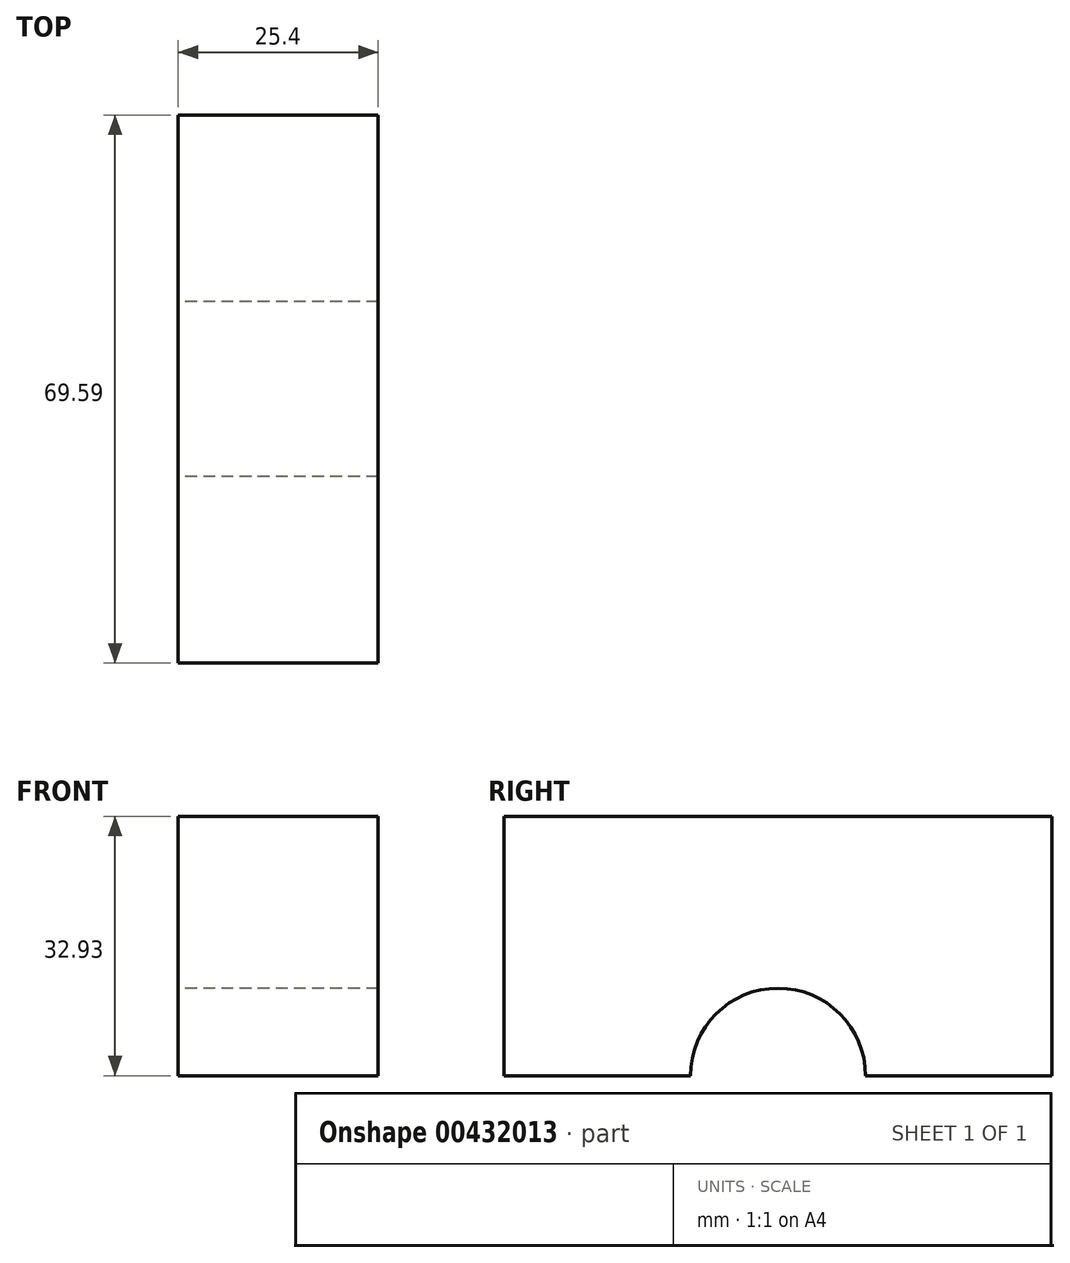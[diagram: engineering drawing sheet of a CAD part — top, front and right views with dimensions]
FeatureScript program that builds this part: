
annotation { "Feature Type Name" : "Feature", "Feature Type Description" : "" }
export const myFeature = defineFeature(function(context is Context, id is Id, definition is map)
    precondition{}
    {
        {
            var Q0;
            Q0=qCreatedBy(makeId("Right.planeOp"),FACE);
            var sketch = newSketch(context, id + "F0", { "sketchPlane" : qUnion([Q0])});
            skLineSegment(sketch, "E0.bottom", {"start": v(0, 0) * mm, "end": v(69.59, 0) * mm});
            skLineSegment(sketch, "E0.top", {"start": v(0, 32.93) * mm, "end": v(69.59, 32.93) * mm});
            skLineSegment(sketch, "E0.left", {"start": v(0, 0) * mm, "end": v(0, 32.93) * mm});
            skLineSegment(sketch, "E0.right", {"start": v(69.59, 0) * mm, "end": v(69.59, 32.93) * mm});
            skSolve(sketch);
        }
        {
            var Q0;
            Q0 = qSketchRegion(id + "F0", true);
            extrude(context, id + "F1", {"entities" : qUnion([Q0]), "depth" : 25.4 * mm});
        }
        {
            var Q0;
            Q0=makeQuery(id+"F1.opExtrude","CAP_FACE",FACE,{"disambiguationData":[OSD([sQuery(id+"F0.wireOp",EDGE,"E0.bottom"),sQuery(id+"F0.wireOp",EDGE,"E0.top"),sQuery(id+"F0.wireOp",EDGE,"E0.left"),sQuery(id+"F0.wireOp",EDGE,"E0.right")])],"isStart":true});
            var sketch = newSketch(context, id + "F2", { "sketchPlane" : qUnion([Q0])});
            skLineSegment(sketch, "E1", {"start": v(-34.8, 0) * mm, "end": v(-34.8, 3.7) * mm});
            skSolve(sketch);
        }
        {
            var Q0;
            Q0=sQuery(id+"F2.wireOp",VERTEX,"E1.start");
            var Q1;
            Q1=makeQuery(id+"F1.opExtrude","SWEPT_BODY",BODY,{"disambiguationData":[OSD([sQuery(id+"F0.wireOp",EDGE,"E0.bottom"),sQuery(id+"F0.wireOp",EDGE,"E0.top"),sQuery(id+"F0.wireOp",EDGE,"E0.left"),sQuery(id+"F0.wireOp",EDGE,"E0.right")])]});
            hole(context, id + "F3", {"style" : HoleStyle.SIMPLE, "endStyle" : HoleEndStyle.THROUGH, "holeDiameter" : 22.22 * mm, "isTappedThrough" : true, "tappedDepth" : 12.7 * mm, "tapClearance" : 3, "locations" : qUnion([Q0]), "scope" : qUnion([Q1])});
        }
    });
